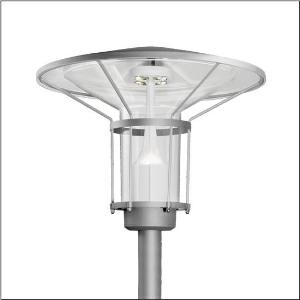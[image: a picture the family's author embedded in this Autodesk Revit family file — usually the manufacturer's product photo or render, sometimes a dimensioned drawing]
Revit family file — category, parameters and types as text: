
# Revit family: laterne_classic___st1_2a_5xa5243ab14h_e952
name_source: partatom
category: Lighting Fixtures
units: mm (PartAtom-declared; Revit-internal decimal feet)

## family parameters
Cut with Voids When Loaded = No
Host = Face
Light Source = No
Part Type = Normal
Room Calculation Point = No
Round Connector Dimension = Use Diameter
Shared = No

## types (1)
- --- (1 x LED, 1380 lm, 14.9 W, 2200K)
    Apparent Load = 15 VA
    CIE Flux Codes = 21 60 93 97 100
    Color Rendering = 70
    Color Temperature = 2200K
    Default Elevation = 1800 mm
    Description = Lantern Classic, mast luminaire, Module 540 Plus, primary light control with 3 zone facetted reflector, of plastic, silver coated, highly specular, structured, primary optical cover: cover, of PMMA, transparent, light distribution: ST1.2a, light emission: direct distribution, primary light characteristic: asymmetric, installation type: post-top, LED, High Power LED, rated luminous flux: 1.380lm, luminous efficacy: 93lm/W, light colour: 722, colour temperature: 2200K, control gear: ECG Plus, control: flexible luminous flux parameterisation, time-dependent luminous flux control, digital communication interface, power reduction, overheat protection, constant luminous flux control, electronic power reduction, with terminal, 6-pole, max. 2.5mm², mains connection: 230..240V, AC, 50/60Hz, start of lifetime: 15W, end of service life: 16W, reduction: 7W, luminaire housing, upper part, of glass-fibre reinforced polyester, coated, Siteco® metallic grey (DB 702S), diameter: 750mm, height: 596mm, spigot size: d x l = 76 x 70mm (post-top) | with reducer (optional accessory) 60 x 70mm, post-top mast mounting element, of diecast aluminium, coated, Siteco® metallic grey (DB 702S), Module 540 Plus, traffic white (RAL 9016), equipment: standard, protection rating (complete): IP65, insulation class (complete): insulation class II (safety insulation), certification: CE, ENEC, VDE, packaging unit: 1 piece

Light Distribution: ST1.2a
    Height = 596 mm
    Lamp = 1 x LED
    Lamp Light Flux = 1380 lm
    Lamp Power = 14.9 W
    Lamp count = 1
    Length = 750 mm
    Luminous efficacy = 93 lm/W
    Manufacturer = Siteco
    ModVariant = No
    Model = 5XA5243AB14H
    Number of Poles = 1
    OnlyDefault = Yes
    Power Factor = 1
    Product Name = Laterne Classic | ST1.2a
    Product group = mast luminaire | pylon top
    ProductGroupID = 6100
    Protection Class = Protection class II
    Protection Degree = IP 65
    RLX_Detail_Level = 1
    RLX_Emergency_Light_Flux = 0 lm
    RLX_Emergency_Type = 0
    RLX_Emergency_Type_DB = No
    RlxData = <blob elided: 92917 chars, md5=b7716700>
    Socket = socket
    Standby Power = 0 W
    System Light Flux = 1380 lm
    System Power = 15 W
    Type Comments = factory setting: luminous flux: 100 % | dim-lin: 254 | 570 mA
    Type Image = l_1006052.jpg
    URL = http://relux.com
    VarID = @adj_155904
    Voltage = 0 V
    Weight = 0.00 kg
    Width = 0 mm  [stored 0 ft]

note: [stored X ft] marks values corroborated as IEEE doubles in the binary element streams (Revit-internal decimal feet)

## geometry (parser evidence)
native form markers: Blend x4, Sweep x10
no freeform markers — native parametric forms only
